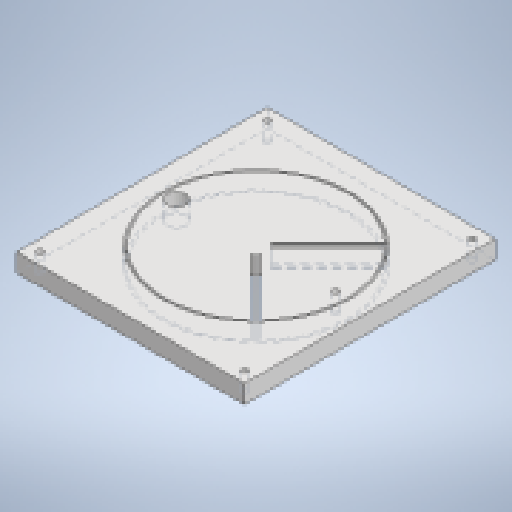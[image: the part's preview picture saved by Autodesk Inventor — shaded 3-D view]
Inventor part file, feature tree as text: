
AUTODESK INVENTOR PART (.ipt)
format: ipt  version: 2023 (Build 270158000, 158)  size: 237,056 bytes
history: native  units: mm
features: extrude x3, sketch x3
ambient origin geometry x8: Origin, YZ Plane, XZ Plane, XY Plane, X Axis, Y Axis, Z Axis, Center Point
bodies: Solid1 (feature_tree)
feature tree (6):
  extrude  "Extrusion1"  Depth=110.0mm
  extrude  "Extrusion2"  TaperAngle=0.0deg  [1 undecoded]
  extrude  "Extrusion5"  Depth=4.0mm
  sketch  "Sketch9"  dims[d4=150.0mm d5=150.0mm d6=8.0mm d7=0.0mm d18=45.0mm d19=45.0mm d21=47.0mm d22=47.0mm d85=20.0mm d86=0.0mm d118=5.0mm d119=5.0mm d120=2.65mm d132=50.0mm d133=55.0mm d134=10.0mm d135=80.0mm d136=82.0mm d145=35.0mm d146=0.0mm d147=2.75mm d153=20.0mm d154=0.0mm d155=8.0mm d156=35.0mm d157=45.0deg d158=0.5mm d159=0.5mm d160=1.0mm d161=1.0mm d162=20.0mm d164=90.0deg d166=1.0mm d167=1.0mm d168=1.0mm d169=30.0mm d170=10.0mm d171=3.0mm d172=5.0mm d173=6.5mm d174=1.0mm d175=0.5mm d176=30.0mm d177=15.0mm d178=4.0mm]
  sketch  "Sketch1"  dims[d0=100.0mm d1=110.0mm]
  sketch  "Sketch8"  dims[d2=0.0mm d3=0.0mm]
note: 1 required parameter value undecoded (feature->parameter linkage not recoverable at this tier; creation-order binding heuristic only, values carry confidence <= 0.55)
